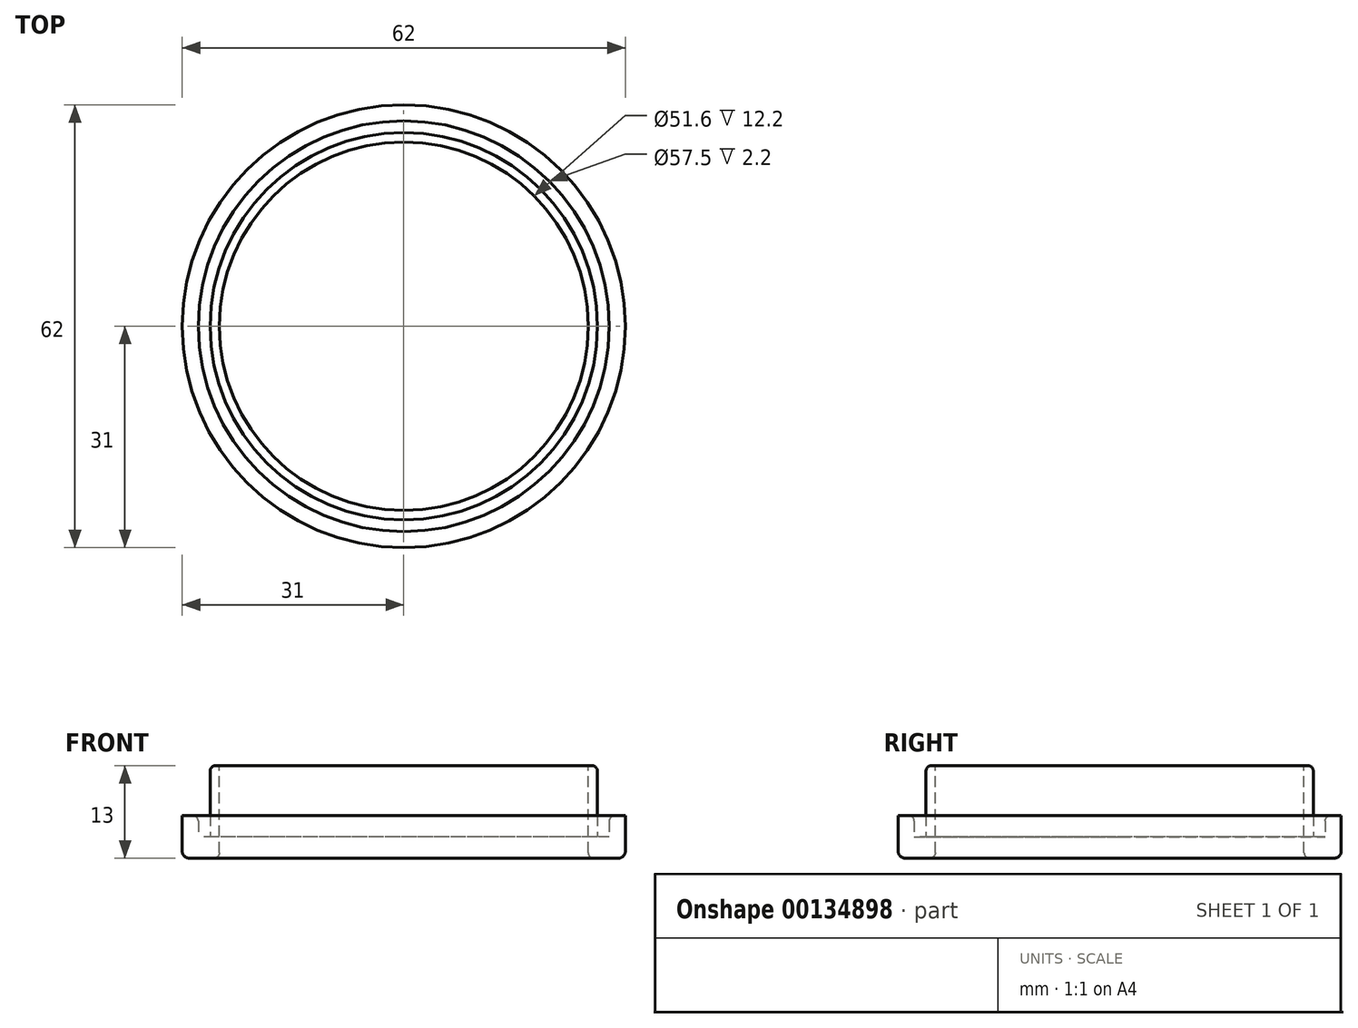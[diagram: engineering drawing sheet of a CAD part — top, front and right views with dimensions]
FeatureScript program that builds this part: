
annotation { "Feature Type Name" : "Feature", "Feature Type Description" : "" }
export const myFeature = defineFeature(function(context is Context, id is Id, definition is map)
    precondition{}
    {
        {
            var Q0;
            Q0=qCreatedBy(makeId("Top.planeOp"),FACE);
            var sketch = newSketch(context, id + "F0", { "sketchPlane" : qUnion([Q0])});
            skCircle(sketch, "E0", {"center": v(0, 0) * mm, "radius": 31 * mm});
            skCircle(sketch, "E1", {"center": v(0, 0) * mm, "radius": 27.1 * mm});
            skCircle(sketch, "E2", {"center": v(0, 0) * mm, "radius": 25.8 * mm});
            skCircle(sketch, "E3", {"center": v(0, 0) * mm, "radius": 28.75 * mm});
            skSolve(sketch);
        }
        {
            var Q0;
            Q0=makeQuery(id+"F0.imprint","IMPRINT",FACE,{"disambiguationData":[TD([[makeQuery(id+"F0.imprint","IMPRINT",EDGE,{"derivedFrom":sQuery(id+"F0.wireOp",EDGE,"E1")}),1.0]])]});
            var Q1;
            Q1=makeQuery(id+"F0.imprint","IMPRINT",FACE,{"disambiguationData":[TD([[makeQuery(id+"F0.imprint","IMPRINT",EDGE,{"derivedFrom":sQuery(id+"F0.wireOp",EDGE,"E1")}),-1.0]])]});
            var Q2;
            Q2=makeQuery(id+"F0.imprint","IMPRINT",FACE,{"disambiguationData":[TD([[makeQuery(id+"F0.imprint","IMPRINT",EDGE,{"derivedFrom":sQuery(id+"F0.wireOp",EDGE,"E0")}),1.0]])]});
            extrude(context, id + "F1", {"entities" : qUnion([Q0, Q1, Q2]), "oppositeDirection" : true, "depth" : 3 * mm});
        }
        {
            var Q0;
            Q0=makeQuery(id+"F0.imprint","IMPRINT",FACE,{"disambiguationData":[TD([[makeQuery(id+"F0.imprint","IMPRINT",EDGE,{"derivedFrom":sQuery(id+"F0.wireOp",EDGE,"E1")}),1.0]])]});
            extrude(context, id + "F2", {"entities" : qUnion([Q0]), "operationType" : NewBodyOperationType.ADD, "depth" : 10 * mm});
        }
        {
            var Q0;
            Q0=makeQuery(id+"F0.imprint","IMPRINT",FACE,{"disambiguationData":[TD([[makeQuery(id+"F0.imprint","IMPRINT",EDGE,{"derivedFrom":sQuery(id+"F0.wireOp",EDGE,"E0")}),1.0]])]});
            extrude(context, id + "F3", {"entities" : qUnion([Q0]), "operationType" : NewBodyOperationType.ADD, "depth" : 3 * mm});
        }
        {
            var Q0;
            Q0=makeQuery(id+"F0.imprint","IMPRINT",FACE,{"disambiguationData":[TD([[makeQuery(id+"F0.imprint","IMPRINT",EDGE,{"derivedFrom":sQuery(id+"F0.wireOp",EDGE,"E2")}),1.0]])]});
            extrude(context, id + "F4", {"entities" : qUnion([Q0]), "operationType" : NewBodyOperationType.REMOVE, "depth" : 25 * mm});
        }
        {
            var Q0;
            Q0=makeQuery(id+"F1.opExtrude","CAP_EDGE",EDGE,{"disambiguationData":[OSD([sQuery(id+"F0.wireOp",EDGE,"E2")])],"isStart":false});
            var Q1;
            Q1=makeQuery(id+"F3.opExtrude","CAP_EDGE",EDGE,{"disambiguationData":[OSD([sQuery(id+"F0.wireOp",EDGE,"E3")])],"isStart":false});
            var Q2;
            Q2=makeQuery(id+"F2.opExtrude","CAP_EDGE",EDGE,{"disambiguationData":[OSD([sQuery(id+"F0.wireOp",EDGE,"E1")])],"isStart":false});
            fillet(context, id + "F5", {"entities" : qUnion([Q0, Q1, Q2]), "radius" : 0.8 * mm, "tangentPropagation" : true, "allowEdgeOverflow" : false});
        }
        {
            var Q0;
            Q0=makeQuery(id+"F1.opExtrude","CAP_EDGE",EDGE,{"disambiguationData":[OSD([sQuery(id+"F0.wireOp",EDGE,"E0")])],"isStart":false});
            fillet(context, id + "F6", {"entities" : qUnion([Q0]), "radius" : 1 * mm, "tangentPropagation" : true, "allowEdgeOverflow" : false});
        }
    });
